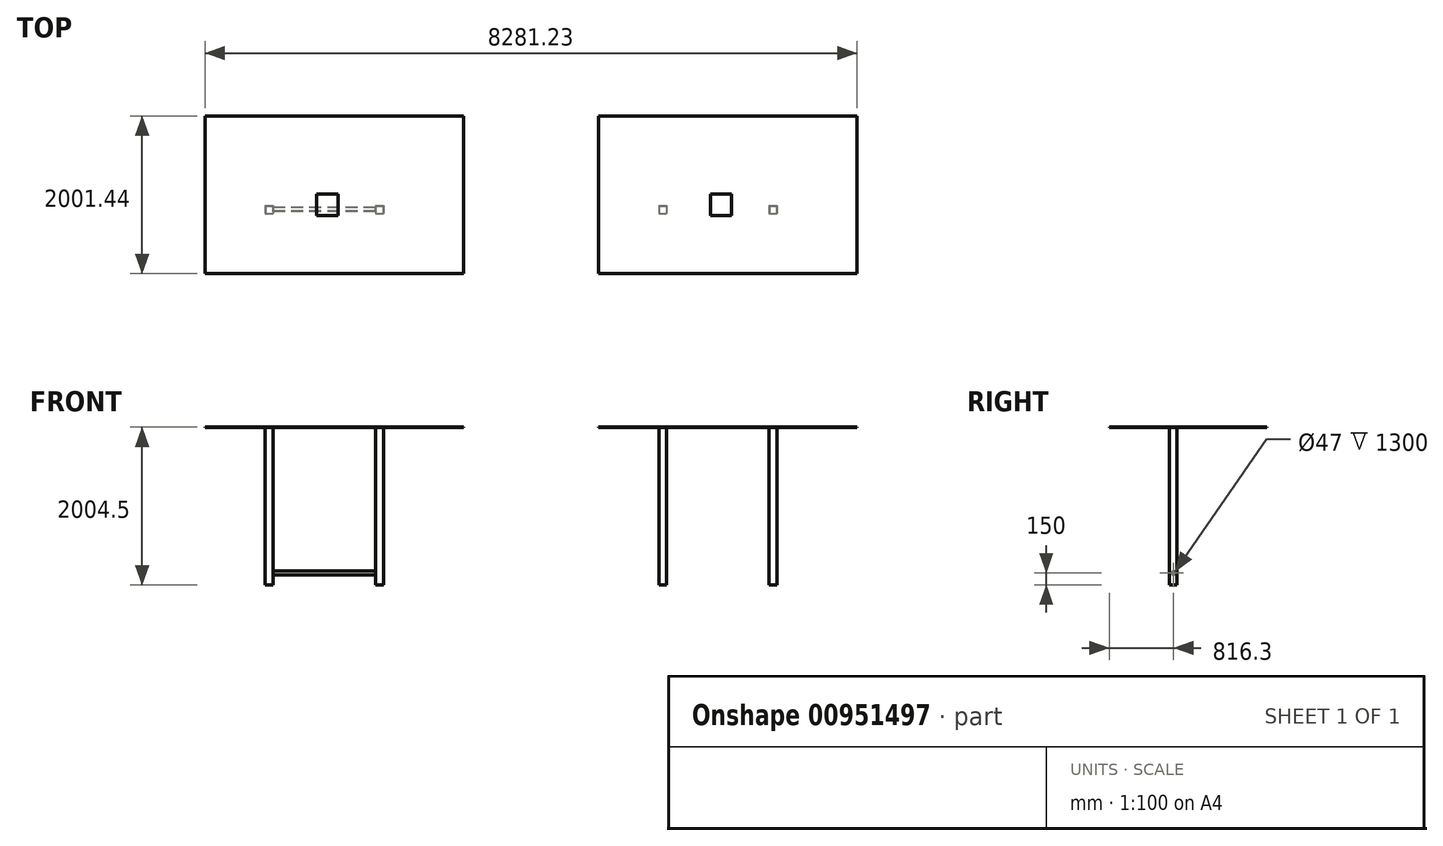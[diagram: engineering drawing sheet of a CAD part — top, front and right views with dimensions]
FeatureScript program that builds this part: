
annotation { "Feature Type Name" : "Feature", "Feature Type Description" : "" }
export const myFeature = defineFeature(function(context is Context, id is Id, definition is map)
    precondition{}
    {
        {
            var Q0;
            Q0=qCreatedBy(makeId("Top.planeOp"),FACE);
            var sketch = newSketch(context, id + "F0", { "sketchPlane" : qUnion([Q0])});
            skLineSegment(sketch, "E0.bottom", {"start": v(-244.1, 45.08) * mm, "end": v(-144.1, 45.08) * mm});
            skLineSegment(sketch, "E0.top", {"start": v(-244.1, -54.92) * mm, "end": v(-144.1, -54.92) * mm});
            skLineSegment(sketch, "E0.left", {"start": v(-244.1, 45.08) * mm, "end": v(-244.1, -54.92) * mm});
            skLineSegment(sketch, "E0.right", {"start": v(-144.1, 45.08) * mm, "end": v(-144.1, -54.92) * mm});
            skLineSegment(sketch, "E1.bottom", {"start": v(1155.9, 45.08) * mm, "end": v(1255.9, 45.08) * mm});
            skLineSegment(sketch, "E1.top", {"start": v(1155.9, -54.92) * mm, "end": v(1255.9, -54.92) * mm});
            skLineSegment(sketch, "E1.left", {"start": v(1155.9, 45.08) * mm, "end": v(1155.9, -54.92) * mm});
            skLineSegment(sketch, "E1.right", {"start": v(1255.9, 45.08) * mm, "end": v(1255.9, -54.92) * mm});
            skLineSegment(sketch, "E2.bottom", {"start": v(1158.9, 42.08) * mm, "end": v(1252.9, 42.08) * mm});
            skLineSegment(sketch, "E2.top", {"start": v(1158.9, -51.92) * mm, "end": v(1252.9, -51.92) * mm});
            skLineSegment(sketch, "E2.left", {"start": v(1158.9, 42.08) * mm, "end": v(1158.9, -51.92) * mm});
            skLineSegment(sketch, "E2.right", {"start": v(1252.9, 42.08) * mm, "end": v(1252.9, -51.92) * mm});
            skLineSegment(sketch, "E3.bottom", {"start": v(-241.1, 42.08) * mm, "end": v(-147.1, 42.08) * mm});
            skLineSegment(sketch, "E3.top", {"start": v(-241.1, -51.92) * mm, "end": v(-147.1, -51.92) * mm});
            skLineSegment(sketch, "E3.left", {"start": v(-241.1, 42.08) * mm, "end": v(-241.1, -51.92) * mm});
            skLineSegment(sketch, "E3.right", {"start": v(-147.1, 42.08) * mm, "end": v(-147.1, -51.92) * mm});
            skSolve(sketch);
        }
        {
            var Q0;
            Q0 = qSketchRegion(id + "F0", true);
            extrude(context, id + "F1", {"entities" : qUnion([Q0]), "depth" : 2000 * mm, "offsetDistance" : 25 * mm});
        }
        {
            var Q0;
            Q0=makeQuery(id+"F1.opExtrude","SWEPT_FACE",FACE,{"disambiguationData":[OSD([sQuery(id+"F0.wireOp",EDGE,"E0.right")])]});
            var sketch = newSketch(context, id + "F2", { "sketchPlane" : qUnion([Q0])});
            skCircle(sketch, "E4", {"center": v(0, 150) * mm, "radius": 25 * mm});
            skLineSegment(sketch, "E5", {"start": v(0, 0) * mm, "end": v(0, 150) * mm, "construction": true});
            skCircle(sketch, "E6", {"center": v(0, 150) * mm, "radius": 23.5 * mm});
            skSolve(sketch);
        }
        {
            var Q0;
            Q0=makeQuery(id+"F2.imprint","IMPRINT",FACE,{"disambiguationData":[TD([[makeQuery(id+"F2.imprint","IMPRINT",EDGE,{"derivedFrom":sQuery(id+"F2.wireOp",EDGE,"E4")}),1.0]])]});
            extrude(context, id + "F3", {"entities" : qUnion([Q0]), "operationType" : NewBodyOperationType.ADD, "endBound" : BoundingType.UP_TO_NEXT, "depth" : 25 * mm, "offsetDistance" : 25 * mm});
        }
        {
            var Q0;
            Q0=makeQuery(id+"F1.opExtrude","CAP_FACE",FACE,{"disambiguationData":[OSD([sQuery(id+"F0.wireOp",EDGE,"E0.bottom"),sQuery(id+"F0.wireOp",EDGE,"E0.top"),sQuery(id+"F0.wireOp",EDGE,"E0.left"),sQuery(id+"F0.wireOp",EDGE,"E0.right")])],"isStart":false});
            var sketch = newSketch(context, id + "F4", { "sketchPlane" : qUnion([Q0])});
            skLineSegment(sketch, "E7.bottom", {"start": v(-1008.17, 1185.14) * mm, "end": v(2273.06, 1185.14) * mm});
            skLineSegment(sketch, "E7.top", {"start": v(-1008.17, -816.3) * mm, "end": v(2273.06, -816.3) * mm});
            skLineSegment(sketch, "E7.left", {"start": v(-1008.17, 1185.14) * mm, "end": v(-1008.17, -816.3) * mm});
            skLineSegment(sketch, "E7.right", {"start": v(2273.06, 1185.14) * mm, "end": v(2273.06, -816.3) * mm});
            skSolve(sketch);
        }
        {
            var Q0;
            Q0 = qSketchRegion(id + "F4", true);
            extrude(context, id + "F5", {"entities" : qUnion([Q0]), "operationType" : NewBodyOperationType.ADD, "depth" : 4 * mm, "offsetDistance" : 25 * mm});
        }
        {
            var Q0;
            Q0=makeQuery(id+"F5.opExtrude","CAP_FACE",FACE,{"disambiguationData":[OSD([sQuery(id+"F4.wireOp",EDGE,"E7.bottom"),sQuery(id+"F4.wireOp",EDGE,"E7.top"),sQuery(id+"F4.wireOp",EDGE,"E7.left"),sQuery(id+"F4.wireOp",EDGE,"E7.right")])],"isStart":false});
            var sketch = newSketch(context, id + "F6", { "sketchPlane" : qUnion([Q0])});
            skLineSegment(sketch, "E8.bottom", {"start": v(410.23, 192.83) * mm, "end": v(680.35, 192.83) * mm});
            skLineSegment(sketch, "E8.top", {"start": v(410.23, -77.29) * mm, "end": v(680.35, -77.29) * mm});
            skLineSegment(sketch, "E8.left", {"start": v(410.23, 192.83) * mm, "end": v(410.23, -77.29) * mm});
            skLineSegment(sketch, "E8.right", {"start": v(680.35, 192.83) * mm, "end": v(680.35, -77.29) * mm});
            skSolve(sketch);
        }
        {
            var Q0;
            Q0 = qSketchRegion(id + "F6", true);
            extrude(context, id + "F7", {"entities" : qUnion([Q0]), "operationType" : NewBodyOperationType.ADD, "depth" : 0.5 * mm, "offsetDistance" : 25 * mm});
        }
        {
            var Q0;
            Q0=makeQuery(id+"F1.opExtrude","SWEPT_BODY",BODY,{"disambiguationData":[OSD([sQuery(id+"F0.wireOp",EDGE,"E0.bottom"),sQuery(id+"F0.wireOp",EDGE,"E0.top"),sQuery(id+"F0.wireOp",EDGE,"E0.left"),sQuery(id+"F0.wireOp",EDGE,"E0.right"),sQuery(id+"F0.wireOp",EDGE,"E3.bottom"),sQuery(id+"F0.wireOp",EDGE,"E3.top"),sQuery(id+"F0.wireOp",EDGE,"E3.left"),sQuery(id+"F0.wireOp",EDGE,"E3.right")])]});
            transform(context, id + "F8", {"entities" : qUnion([Q0]), "transformType" : TransformType.TRANSLATION_3D, "dx" : 5000 * mm, "dy" : 0 * mm, "dz" : 0 * mm, "makeCopy" : true});
        }
        {
            var Q0;
            {var subQ5=sQuery(id+"F0.wireOp",EDGE,"E0.right");var subQ7=sQuery(id+"F0.wireOp",EDGE,"E0.bottom");Q0=makeQuery(id+"F8.opPattern","COPY",FACE,{"derivedFrom":makeQuery(id+"F3.boolean.opBoolean","SPLIT",FACE,{"disambiguationData":[TD([makeQuery(id+"F1.opExtrude","SWEPT_FACE",FACE,{"disambiguationData":[OSD([subQ7])]})])],"derivedFrom":makeQuery(id+"F1.opExtrude","SWEPT_FACE",FACE,{"disambiguationData":[OSD([subQ5])]})}),"instanceName":"1"});}
            var sketch = newSketch(context, id + "F9", { "sketchPlane" : qUnion([Q0])});
            skLineSegment(sketch, "E9.bottom", {"start": v(-439.58, 395.87) * mm, "end": v(460.2, 395.87) * mm});
            skLineSegment(sketch, "E9.top", {"start": v(-439.58, -40.62) * mm, "end": v(460.2, -40.62) * mm});
            skLineSegment(sketch, "E9.left", {"start": v(-439.58, 395.87) * mm, "end": v(-439.58, -40.62) * mm});
            skLineSegment(sketch, "E9.right", {"start": v(460.2, 395.87) * mm, "end": v(460.2, -40.62) * mm});
            skSolve(sketch);
        }
        {
            var Q0;
            Q0 = qSketchRegion(id + "F9", true);
            extrude(context, id + "F10", {"entities" : qUnion([Q0]), "operationType" : NewBodyOperationType.REMOVE, "depth" : 1300 * mm, "offsetDistance" : 25 * mm});
        }
    });
